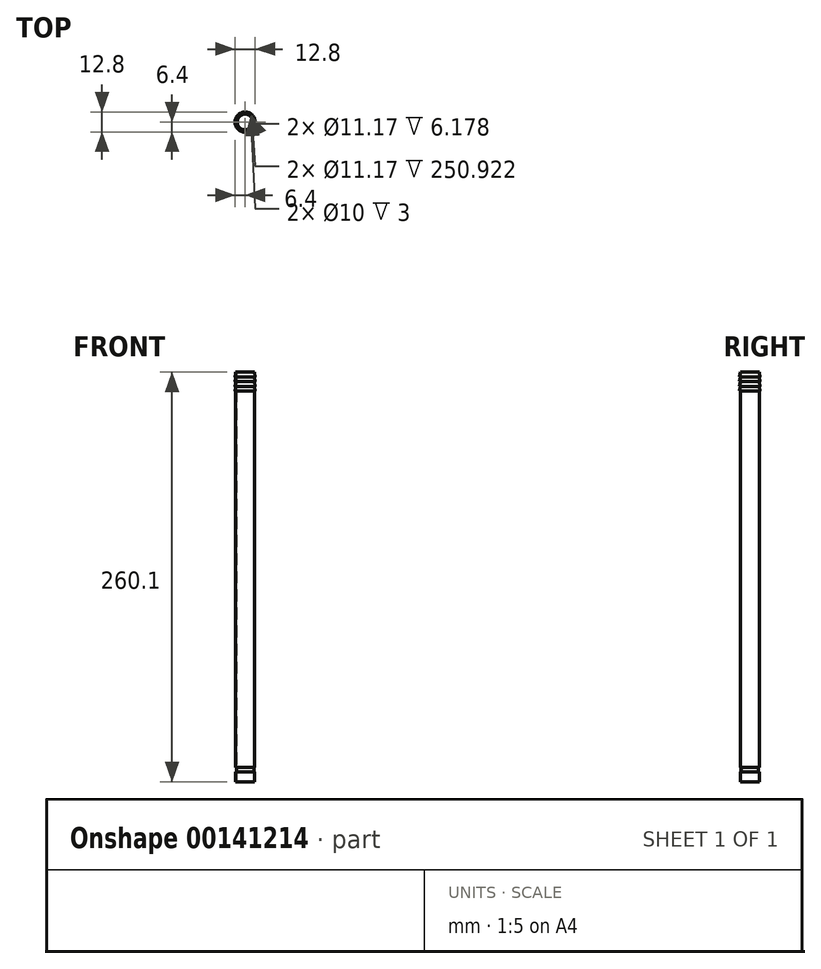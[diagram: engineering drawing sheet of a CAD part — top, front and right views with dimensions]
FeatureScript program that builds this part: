
annotation { "Feature Type Name" : "Feature", "Feature Type Description" : "" }
export const myFeature = defineFeature(function(context is Context, id is Id, definition is map)
    precondition{}
    {
        {
            var Q0;
            Q0=qCreatedBy(makeId("Front.planeOp"),FACE);
            var sketch = newSketch(context, id + "F0", { "sketchPlane" : qUnion([Q0])});
            skLineSegment(sketch, "E0", {"start": v(6, -66.45) * mm, "end": v(6, -60.28) * mm});
            skLineSegment(sketch, "E1", {"start": v(5, -60.28) * mm, "end": v(6, -60.28) * mm});
            skLineSegment(sketch, "E2", {"start": v(5, -60.28) * mm, "end": v(5, -57.28) * mm});
            skLineSegment(sketch, "E3", {"start": v(5, -57.28) * mm, "end": v(6, -57.28) * mm});
            skPoint(sketch, "E4", {"position": v(6, -57.28) * mm});
            skPoint(sketch, "E5", {"position": v(6.08, -60.38) * mm});
            skPoint(sketch, "E6", {"position": v(6, -60.28) * mm});
            skLineSegment(sketch, "E7.trimOffspring", {"start": v(6, -57.28) * mm, "end": v(6, 193.65) * mm});
            skPoint(sketch, "E8", {"position": v(6, 190.65) * mm});
            skPoint(sketch, "E9", {"position": v(6, 187.65) * mm});
            skPoint(sketch, "E10", {"position": v(6, 184.65) * mm});
            skPoint(sketch, "E11", {"position": v(6, 181.65) * mm});
            skLineSegment(sketch, "E12", {"start": v(6, 190.65) * mm, "end": v(6.4, 190.65) * mm});
            skLineSegment(sketch, "E13", {"start": v(6, 193.65) * mm, "end": v(6.4, 190.65) * mm});
            skLineSegment(sketch, "E14", {"start": v(6, 187.65) * mm, "end": v(6.4, 187.65) * mm});
            skLineSegment(sketch, "E15", {"start": v(6, 190.65) * mm, "end": v(6.4, 187.65) * mm});
            skLineSegment(sketch, "E16", {"start": v(6, 184.65) * mm, "end": v(6.4, 184.65) * mm});
            skLineSegment(sketch, "E17", {"start": v(6, 187.65) * mm, "end": v(6.4, 184.65) * mm});
            skLineSegment(sketch, "E18", {"start": v(6, 181.65) * mm, "end": v(6.4, 181.65) * mm});
            skLineSegment(sketch, "E19", {"start": v(6, 184.65) * mm, "end": v(6.4, 181.65) * mm});
            skLineSegment(sketch, "E20", {"start": v(0, -66.28) * mm, "end": v(0, 193.82) * mm});
            skLineSegment(sketch, "E21", {"start": v(6, 193.65) * mm, "end": v(5.58, 193.65) * mm});
            skLineSegment(sketch, "E22", {"start": v(5.58, 193.65) * mm, "end": v(5.58, -66.45) * mm});
            skLineSegment(sketch, "E23", {"start": v(6, -66.45) * mm, "end": v(5.58, -66.45) * mm});
            skSolve(sketch);
        }
        {
            var Q0;
            Q0 = qSketchRegion(id + "F0", true);
            var Q1;
            Q1=sQuery(id+"F0.wireOp",EDGE,"E20");
            revolve(context, id + "F1", {"entities" : qUnion([Q0]), "axis" : qUnion([Q1]), "revolveType" : RevolveType.FULL});
        }
    });
